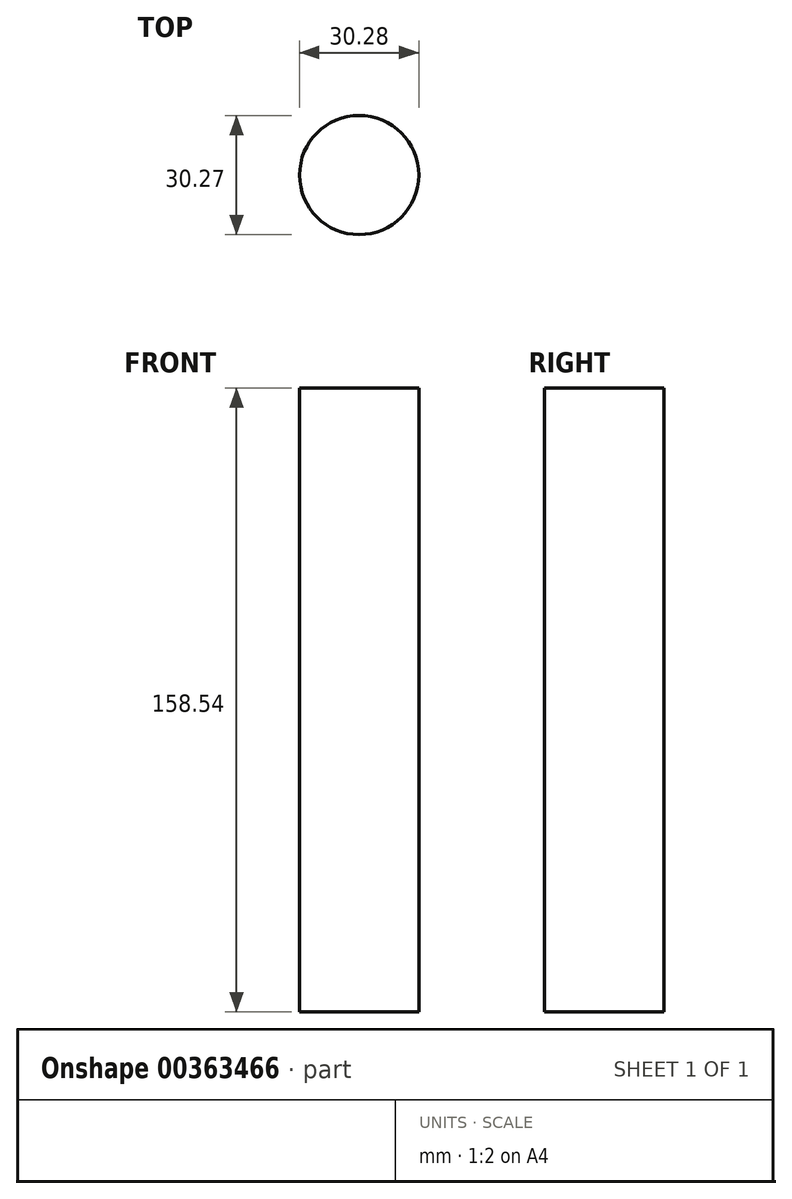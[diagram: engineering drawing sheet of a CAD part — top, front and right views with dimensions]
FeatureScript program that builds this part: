
annotation { "Feature Type Name" : "Feature", "Feature Type Description" : "" }
export const myFeature = defineFeature(function(context is Context, id is Id, definition is map)
    precondition{}
    {
        {
            var Q0;
            Q0=qCreatedBy(makeId("Top.planeOp"),FACE);
            var sketch = newSketch(context, id + "F0", { "sketchPlane" : qUnion([Q0])});
            skLineSegment(sketch, "E0.bottom", {"start": v(37.18, 59.65) * mm, "end": v(13.17, 59.65) * mm});
            skLineSegment(sketch, "E0.top", {"start": v(37.18, 13.56) * mm, "end": v(13.17, 13.56) * mm});
            skLineSegment(sketch, "E0.left", {"start": v(37.18, 59.65) * mm, "end": v(37.18, 13.56) * mm});
            skLineSegment(sketch, "E0.right", {"start": v(13.17, 59.65) * mm, "end": v(13.17, 13.56) * mm});
            skPoint(sketch, "E0.middle", {"position": v(25.17, 36.6) * mm});
            skCircle(sketch, "E1", {"center": v(-28.92, 33.22) * mm, "radius": 15.14 * mm});
            skSolve(sketch);
        }
        {
            var Q0;
            Q0=makeQuery(id+"F0.imprint","IMPRINT",FACE,{"disambiguationData":[TD([[makeQuery(id+"F0.imprint","IMPRINT",EDGE,{"derivedFrom":sQuery(id+"F0.wireOp",EDGE,"E1")}),1.0]])]});
            extrude(context, id + "F1", {"entities" : qUnion([Q0]), "depth" : 158.54 * mm, "offsetDistance" : 25 * mm});
        }
    });
